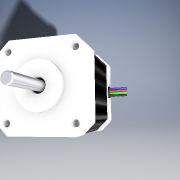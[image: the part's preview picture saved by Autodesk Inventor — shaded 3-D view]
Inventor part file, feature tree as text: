
AUTODESK INVENTOR PART (.ipt)
format: ipt  version: 2016 (Build 200138000, 138)  size: 1,125,376 bytes
history: native  units: mm
features: extrude x12, sketch x4, hole x4, fillet x4, chamfer x2, plane x1, pattern_linear x1, projected_geometry x1
ambient origin geometry x8: Origin, YZ Plane, XZ Plane, XY Plane, X Axis, Y Axis, Z Axis, Center Point
bodies: Solid1 (feature_tree)
feature tree (29):
  sketch  "Sketch1"  dims[d0=7.0mm d1=22.0mm]
  extrude  "Extrusion1"  Depth=22.0mm
  extrude  "Extrusion2"  Depth=31.0mm
  extrude  "Extrusion3"  Depth=3.0mm
  plane  "Work Plane2"
  extrude  "Extrusion7"  Depth=10.0mm
  extrude  "Extrusion8"  Depth=10.0mm
  chamfer  "Chamfer1"  Distance=42.0mm
  pattern_linear  "Rectangular Pattern2"  Spacing1=42.0mm  [1 undecoded]
  hole  "Hole1"  [1 undecoded]
  hole  "Hole2"  [1 undecoded]
  hole  "Hole3"  [1 undecoded]
  hole  "Hole4"  [1 undecoded]
  extrude  "Extrusion9"  Depth=10.0mm
  fillet  "Fillet1"  Radius=24.0mm
  fillet  "Fillet2"  Radius=2.0mm
  chamfer  "Chamfer2"  Distance=48.0mm
  fillet  "Fillet3"  [1 undecoded]
  sketch  "Sketch6"  dims[d10=3.0mm d11=3.0mm d12=3.0mm d39=42.0mm d40=42.0mm d41=135.0deg d42=51.618795mm d43=51.618795mm d44=25.809398mm d45=25.809398mm d46=24.0mm d47=0.0mm d48=2.0mm d49=0.0mm d50=48.0mm d51=0.0mm d60=-10.0mm d126=28.0mm d127=0.0mm d128=1.0mm d129=1.0mm d130=1.0mm d131=1.0mm d132=0.5mm d134=0.5mm d135=0.5mm d136=0.5mm d137=0.5mm d138=1.0mm d139=1.0mm d140=0.5mm d141=0.0mm d145=0.125mm d146=2.0mm d147=45.0deg d148=560.0mm d150=0.5mm d151=10.0mm d152=10.0mm d153=6.0mm d154=6.0mm d155=4.0mm d156=2.0mm d157=90.0deg d158=3.0mm d159=0.0mm d160=10.0mm d161=10.0mm d162=6.0mm d163=6.0mm d164=4.0mm d165=2.0mm d166=90.0deg d167=3.0mm d168=0.0mm d169=10.0mm d170=10.0mm d171=6.0mm d172=6.0mm d173=4.0mm d174=2.0mm d175=90.0deg d176=3.0mm d177=0.0mm d178=10.0mm d179=10.0mm d180=6.0mm d181=6.0mm d182=4.0mm d183=2.0mm d184=90.0deg d185=3.0mm d186=0.0mm d187=48.0mm d188=0.0mm d189=47.0mm d190=0.0mm d191=1.0mm d192=1.0mm d193=0.5mm d194=2.0mm d195=45.0deg d196=0.5mm d197=1.2mm d198=40.0mm d200=1.2mm d201=10.0mm d203=10.0mm d205=2.5mm d206=2.5mm d207=1.0mm d208=0.0mm d209=0.3mm d210=10.0mm d211=0.0mm d212=10.0mm d213=0.0mm d214=10.0mm d215=0.0mm d216=10.0mm d217=0.0mm d218=0.2mm d219=5.0mm d220=0.0mm d221=0.0mm]
  extrude  "Extrusion10"  Depth=10.0mm TaperAngle=0.0deg
  fillet  "Fillet4"  Radius=1.0mm
  extrude  "Extrusion11"  Depth=10.0mm
  extrude  "Extrusion12"  Depth=10.0mm
  extrude  "Extrusion13"  Depth=10.0mm
  extrude  "Extrusion14"  Depth=10.0mm
  extrude  "Extrusion15"  Depth=10.0mm
  sketch  "Sketch4"  dims[d4=5.0mm d5=31.0mm]
  projected_geometry  "Projected Loop2"
  sketch  "Sketch5"  dims[d6=31.0mm d9=3.0mm]
note: 6 required parameter values undecoded (feature->parameter linkage not recoverable at this tier; creation-order binding heuristic only, values carry confidence <= 0.55)
